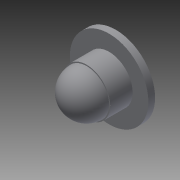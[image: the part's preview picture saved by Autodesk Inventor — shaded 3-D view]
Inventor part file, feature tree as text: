
AUTODESK INVENTOR PART (.ipt)
format: ipt  version: 2014 (Build 180170000, 170)  size: 108,544 bytes
history: native  units: mm
features: sketch x4, revolve x2, extrude x2, plane x1
ambient origin geometry x8: Origin, YZ Plane, XZ Plane, XY Plane, X Axis, Y Axis, Z Axis, Center Point
bodies: Solid1 (feature_tree)
feature tree (9):
  revolve  "Revolution1"  Angle=90.0deg
  plane  "Work Plane1"
  sketch  "Sketch2"  dims[d2=21.0mm d3=21.0mm]
  revolve  "Revolution2"  [1 undecoded]
  extrude  "Extrusion1"  Depth=10.0mm TaperAngle=0.0deg
  extrude  "Extrusion2"  Depth=3.0mm TaperAngle=0.0deg
  sketch  "Sketch1"  dims[d0=20.0mm d1=90.0deg]
  sketch  "Sketch3"  dims[d4=180.0deg d5=10.0mm d6=0.0mm]
  sketch  "Sketch4"  dims[d7=35.0mm d8=3.0mm d9=0.0mm]
note: 1 required parameter value undecoded (feature->parameter linkage not recoverable at this tier; creation-order binding heuristic only, values carry confidence <= 0.55)
